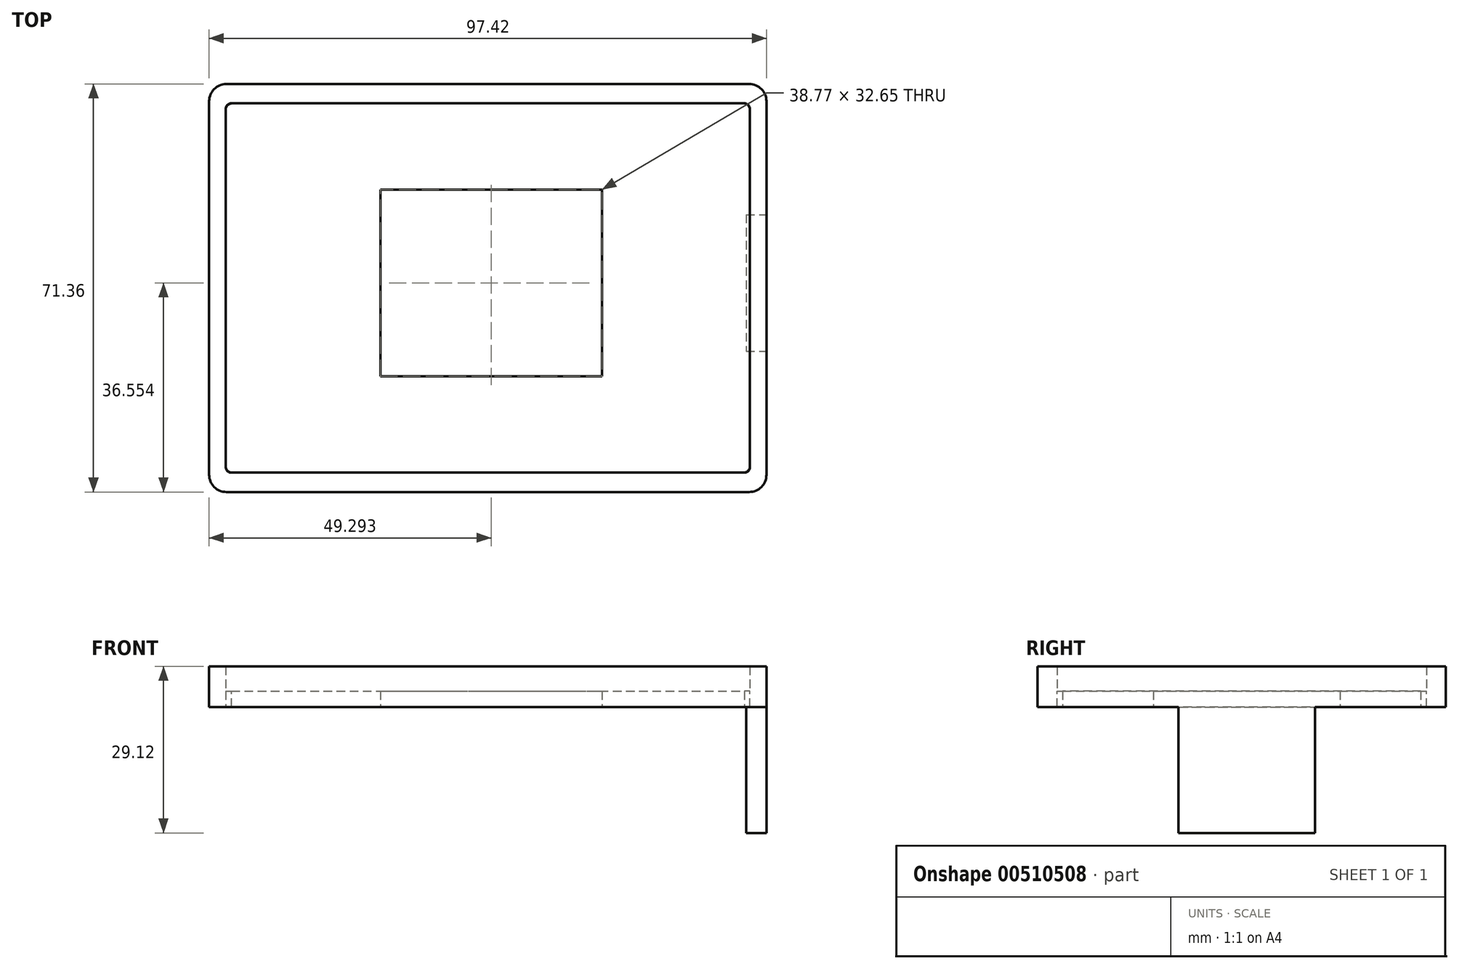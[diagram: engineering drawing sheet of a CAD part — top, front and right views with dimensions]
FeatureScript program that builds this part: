
annotation { "Feature Type Name" : "Feature", "Feature Type Description" : "" }
export const myFeature = defineFeature(function(context is Context, id is Id, definition is map)
    precondition{}
    {
        {
            var Q0;
            Q0=qCreatedBy(makeId("Top.planeOp"),FACE);
            var sketch = newSketch(context, id + "F0", { "sketchPlane" : qUnion([Q0])});
            skLineSegment(sketch, "E0.bottom", {"start": v(-44.83, -32.3) * mm, "end": v(44.83, -32.3) * mm});
            skLineSegment(sketch, "E0.top", {"start": v(-44.83, 32.3) * mm, "end": v(44.83, 32.3) * mm});
            skLineSegment(sketch, "E0.left", {"start": v(-45.83, -31.3) * mm, "end": v(-45.83, 31.3) * mm});
            skLineSegment(sketch, "E0.right", {"start": v(45.83, -31.3) * mm, "end": v(45.83, 31.3) * mm});
            skPoint(sketch, "E0.middle", {"position": v(0, 0) * mm});
            skPoint(sketch, "E1.visualSharp", {"position": v(-45.83, 32.3) * mm});
            skArc(sketch, "E1.filletArc", {"start": v(-44.83, 32.3) * mm, "mid": v(-45.54, 32) * mm, "end": v(-45.83, 31.3) * mm});
            skPoint(sketch, "E2.visualSharp", {"position": v(-45.83, -32.3) * mm});
            skArc(sketch, "E2.filletArc", {"start": v(-45.83, -31.3) * mm, "mid": v(-45.54, -32) * mm, "end": v(-44.83, -32.3) * mm});
            skPoint(sketch, "E3.visualSharp", {"position": v(45.83, -32.3) * mm});
            skArc(sketch, "E3.filletArc", {"start": v(44.83, -32.3) * mm, "mid": v(45.54, -32) * mm, "end": v(45.83, -31.3) * mm});
            skPoint(sketch, "E4.visualSharp", {"position": v(45.83, 32.3) * mm});
            skArc(sketch, "E4.filletArc", {"start": v(45.83, 31.3) * mm, "mid": v(45.54, 32) * mm, "end": v(44.83, 32.3) * mm});
            skLineSegment(sketch, "E5.bottom", {"start": v(45.71, 35.68) * mm, "end": v(-45.71, 35.68) * mm});
            skLineSegment(sketch, "E5.top", {"start": v(45.71, -35.68) * mm, "end": v(-45.71, -35.68) * mm});
            skLineSegment(sketch, "E5.left", {"start": v(48.71, 32.68) * mm, "end": v(48.71, -32.68) * mm});
            skLineSegment(sketch, "E5.right", {"start": v(-48.71, 32.68) * mm, "end": v(-48.71, -32.68) * mm});
            skPoint(sketch, "E6.visualSharp", {"position": v(-48.71, -35.68) * mm});
            skArc(sketch, "E6.filletArc", {"start": v(-48.71, -32.68) * mm, "mid": v(-47.83, -34.8) * mm, "end": v(-45.71, -35.68) * mm});
            skPoint(sketch, "E7.visualSharp", {"position": v(-48.71, 35.68) * mm});
            skArc(sketch, "E7.filletArc", {"start": v(-45.71, 35.68) * mm, "mid": v(-47.83, 34.8) * mm, "end": v(-48.71, 32.68) * mm});
            skPoint(sketch, "E8.visualSharp", {"position": v(48.71, 35.68) * mm});
            skArc(sketch, "E8.filletArc", {"start": v(48.71, 32.68) * mm, "mid": v(47.83, 34.8) * mm, "end": v(45.71, 35.68) * mm});
            skPoint(sketch, "E9.visualSharp", {"position": v(48.71, -35.68) * mm});
            skArc(sketch, "E9.filletArc", {"start": v(45.71, -35.68) * mm, "mid": v(47.83, -34.8) * mm, "end": v(48.71, -32.68) * mm});
            skLineSegment(sketch, "E10.bottom", {"start": v(-44.69, 32.3) * mm, "end": v(44.69, 32.3) * mm});
            skLineSegment(sketch, "E10.top", {"start": v(-44.69, -32.3) * mm, "end": v(44.69, -32.3) * mm});
            skLineSegment(sketch, "E10.left", {"start": v(-45.83, 31.16) * mm, "end": v(-45.83, -31.16) * mm});
            skLineSegment(sketch, "E10.right", {"start": v(45.83, 31.16) * mm, "end": v(45.83, -31.16) * mm});
            skArc(sketch, "E11.filletArc", {"start": v(-44.69, 32.3) * mm, "mid": v(-45.5, 31.97) * mm, "end": v(-45.83, 31.16) * mm});
            skArc(sketch, "E12.filletArc", {"start": v(45.83, 31.16) * mm, "mid": v(45.5, 31.97) * mm, "end": v(44.69, 32.3) * mm});
            skArc(sketch, "E13.filletArc", {"start": v(44.69, -32.3) * mm, "mid": v(45.5, -31.97) * mm, "end": v(45.83, -31.16) * mm});
            skArc(sketch, "E14.filletArc", {"start": v(-45.83, -31.16) * mm, "mid": v(-45.5, -31.97) * mm, "end": v(-44.69, -32.3) * mm});
            skSolve(sketch);
        }
        {
            var Q0;
            Q0=makeQuery(id+"F0.imprint","IMPRINT",FACE,{"disambiguationData":[TD([[makeQuery(id+"F0.imprint","IMPRINT",EDGE,{"derivedFrom":sQuery(id+"F0.wireOp",EDGE,"E0.bottom")}),-1.0]])]});
            extrude(context, id + "F1", {"entities" : qUnion([Q0]), "depth" : 7.11 * mm, "offsetDistance" : 25.4 * mm});
        }
        {
            var Q0;
            Q0=qCreatedBy(makeId("Top.planeOp"),FACE);
            var sketch = newSketch(context, id + "F2", { "sketchPlane" : qUnion([Q0])});
            skLineSegment(sketch, "E15.bottom", {"start": v(-44.69, 32.3) * mm, "end": v(44.69, 32.3) * mm});
            skLineSegment(sketch, "E15.top", {"start": v(-44.69, -32.3) * mm, "end": v(44.69, -32.3) * mm});
            skLineSegment(sketch, "E15.left", {"start": v(-45.83, 31.16) * mm, "end": v(-45.83, -31.16) * mm});
            skLineSegment(sketch, "E15.right", {"start": v(45.83, 31.16) * mm, "end": v(45.83, -31.16) * mm});
            skPoint(sketch, "E16.visualSharp", {"position": v(-45.83, 32.3) * mm});
            skArc(sketch, "E16.filletArc", {"start": v(-44.69, 32.3) * mm, "mid": v(-45.5, 31.97) * mm, "end": v(-45.83, 31.16) * mm});
            skPoint(sketch, "E17.visualSharp", {"position": v(45.83, 32.3) * mm});
            skArc(sketch, "E17.filletArc", {"start": v(45.83, 31.16) * mm, "mid": v(45.5, 31.97) * mm, "end": v(44.69, 32.3) * mm});
            skPoint(sketch, "E18.visualSharp", {"position": v(-45.83, -32.3) * mm});
            skArc(sketch, "E18.filletArc", {"start": v(-45.83, -31.16) * mm, "mid": v(-45.5, -31.97) * mm, "end": v(-44.69, -32.3) * mm});
            skPoint(sketch, "E19.visualSharp", {"position": v(45.83, -32.3) * mm});
            skArc(sketch, "E19.filletArc", {"start": v(44.69, -32.3) * mm, "mid": v(45.5, -31.97) * mm, "end": v(45.83, -31.16) * mm});
            skLineSegment(sketch, "E20.bottom", {"start": v(-18.8, -15.45) * mm, "end": v(19.97, -15.45) * mm});
            skLineSegment(sketch, "E20.top", {"start": v(-18.8, 17.2) * mm, "end": v(19.97, 17.2) * mm});
            skLineSegment(sketch, "E20.left", {"start": v(-18.8, -15.45) * mm, "end": v(-18.8, 17.2) * mm});
            skLineSegment(sketch, "E20.right", {"start": v(19.97, -15.45) * mm, "end": v(19.97, 17.2) * mm});
            skSolve(sketch);
        }
        {
            var Q0;
            Q0=makeQuery(id+"F2.imprint","IMPRINT",FACE,{"disambiguationData":[TD([[makeQuery(id+"F2.imprint","IMPRINT",EDGE,{"derivedFrom":sQuery(id+"F2.wireOp",EDGE,"E15.bottom")}),-1.0]])]});
            extrude(context, id + "F3", {"entities" : qUnion([Q0]), "operationType" : NewBodyOperationType.ADD, "depth" : 2.8 * mm, "offsetDistance" : 25.4 * mm});
        }
        {
            var Q0;
            Q0=makeQuery(id+"F1.opExtrude","SWEPT_FACE",FACE,{"disambiguationData":[OSD([sQuery(id+"F0.wireOp",EDGE,"E5.left")])]});
            var sketch = newSketch(context, id + "F4", { "sketchPlane" : qUnion([Q0])});
            skLineSegment(sketch, "E21.bottom", {"start": v(-11.08, 5.2) * mm, "end": v(12.82, 5.2) * mm});
            skLineSegment(sketch, "E21.top", {"start": v(-11.08, -22) * mm, "end": v(12.82, -22) * mm});
            skLineSegment(sketch, "E21.left", {"start": v(-11.08, 5.2) * mm, "end": v(-11.08, -22) * mm});
            skLineSegment(sketch, "E21.right", {"start": v(12.82, 5.2) * mm, "end": v(12.82, -22) * mm});
            skSolve(sketch);
        }
        {
            var Q0;
            {var subQ0=sQuery(id+"F4.wireOp",EDGE,"E21.top");Q0=makeQuery(id+"F4.imprint","IMPRINT",FACE,{"disambiguationData":[TD([[makeQuery(id+"F4.imprint","IMPRINT",EDGE,{"derivedFrom":subQ0}),1.0]])]});}
            extrude(context, id + "F5", {"entities" : qUnion([Q0]), "operationType" : NewBodyOperationType.ADD, "oppositeDirection" : true, "depth" : 3.56 * mm, "offsetDistance" : 25.4 * mm});
        }
    });
